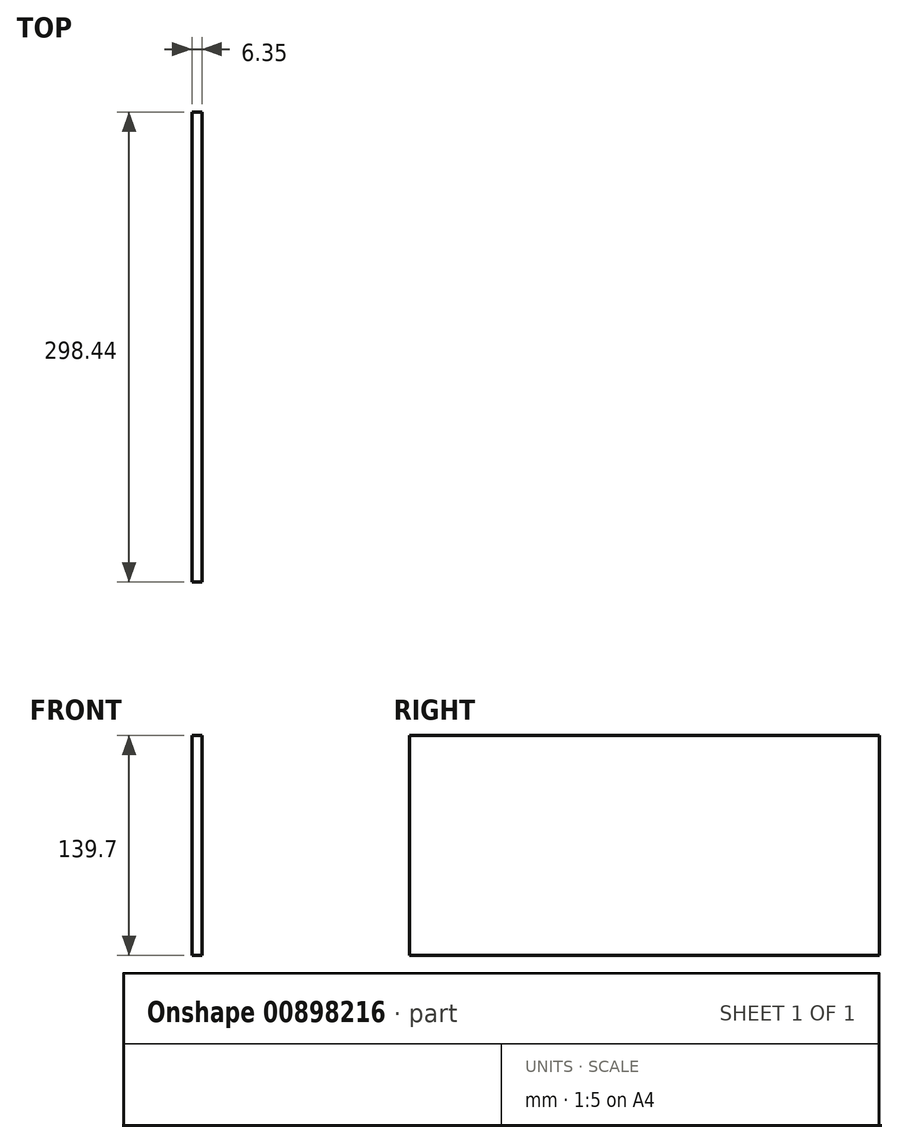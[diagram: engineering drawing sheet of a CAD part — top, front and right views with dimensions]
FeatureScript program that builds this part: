
annotation { "Feature Type Name" : "Feature", "Feature Type Description" : "" }
export const myFeature = defineFeature(function(context is Context, id is Id, definition is map)
    precondition{}
    {
        {
            var Q0;
            Q0=qCreatedBy(makeId("Right.planeOp"),FACE);
            var sketch = newSketch(context, id + "F0", { "sketchPlane" : qUnion([Q0])});
            skLineSegment(sketch, "E0.bottom", {"start": v(-149.22, 69.85) * mm, "end": v(149.22, 69.85) * mm});
            skLineSegment(sketch, "E0.top", {"start": v(-149.23, -69.85) * mm, "end": v(149.22, -69.85) * mm});
            skLineSegment(sketch, "E0.left", {"start": v(-149.22, 69.85) * mm, "end": v(-149.23, -69.85) * mm});
            skLineSegment(sketch, "E0.right", {"start": v(149.22, 69.85) * mm, "end": v(149.22, -69.85) * mm});
            skPoint(sketch, "E0.middle", {"position": v(0, 0) * mm});
            skSolve(sketch);
        }
        {
            var Q0;
            Q0 = qSketchRegion(id + "F0", true);
            extrude(context, id + "F1", {"entities" : qUnion([Q0]), "oppositeDirection" : true, "depth" : 6.35 * mm, "offsetDistance" : 25.4 * mm});
        }
    });
